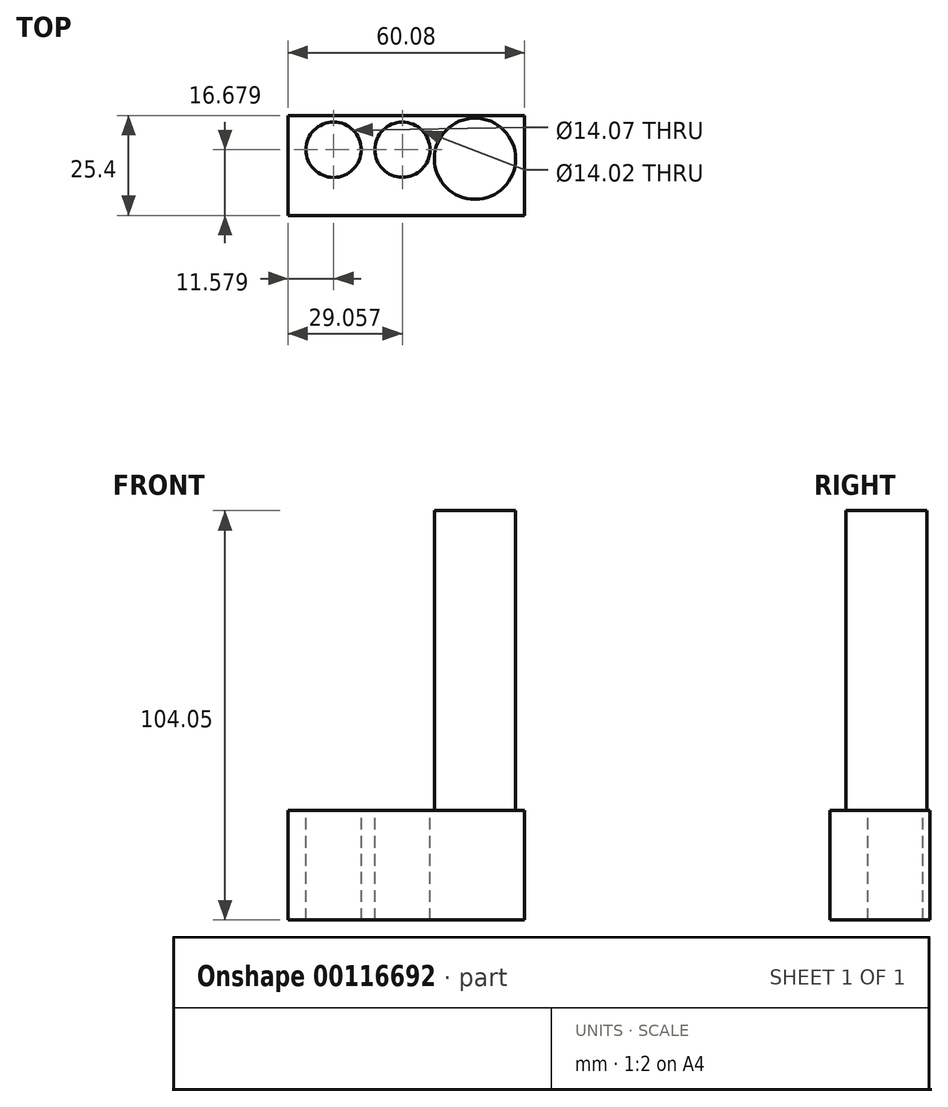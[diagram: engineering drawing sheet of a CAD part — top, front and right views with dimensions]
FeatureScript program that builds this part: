
annotation { "Feature Type Name" : "Feature", "Feature Type Description" : "" }
export const myFeature = defineFeature(function(context is Context, id is Id, definition is map)
    precondition{}
    {
        {
            var Q0;
            Q0=qCreatedBy(makeId("Front.planeOp"),FACE);
            var sketch = newSketch(context, id + "F0", { "sketchPlane" : qUnion([Q0])});
            skLineSegment(sketch, "E0.bottom", {"start": v(-24.03, 15.02) * mm, "end": v(36.05, 15.02) * mm});
            skLineSegment(sketch, "E0.top", {"start": v(-24.03, -12.83) * mm, "end": v(36.05, -12.83) * mm});
            skLineSegment(sketch, "E0.left", {"start": v(-24.03, 15.02) * mm, "end": v(-24.03, -12.83) * mm});
            skLineSegment(sketch, "E0.right", {"start": v(36.05, 15.02) * mm, "end": v(36.05, -12.83) * mm});
            skSolve(sketch);
        }
        {
            var Q0;
            Q0=makeQuery(id+"F0.imprint","IMPRINT",FACE,{"disambiguationData":[TD([[makeQuery(id+"F0.imprint","IMPRINT",EDGE,{"derivedFrom":sQuery(id+"F0.wireOp",EDGE,"E0.bottom")}),-1.0]])]});
            extrude(context, id + "F1", {"entities" : qUnion([Q0]), "depth" : 25.4 * mm});
        }
        {
            var Q0;
            Q0=makeQuery(id+"F1.opExtrude","SWEPT_FACE",FACE,{"disambiguationData":[OSD([sQuery(id+"F0.wireOp",EDGE,"E0.bottom")])]});
            var sketch = newSketch(context, id + "F2", { "sketchPlane" : qUnion([Q0])});
            skCircle(sketch, "E1", {"center": v(-12.45, -8.72) * mm, "radius": 7.04 * mm});
            skCircle(sketch, "E2", {"center": v(5.03, -8.72) * mm, "radius": 7.01 * mm});
            skCircle(sketch, "E3", {"center": v(24.03, -16.87) * mm, "radius": 3.87 * mm});
            skSolve(sketch);
        }
        {
            var Q0;
            Q0=makeQuery(id+"F2.imprint","IMPRINT",FACE,{"disambiguationData":[TD([[makeQuery(id+"F2.imprint","IMPRINT",EDGE,{"derivedFrom":sQuery(id+"F2.wireOp",EDGE,"E2")}),1.0]])]});
            var Q1;
            Q1=makeQuery(id+"F2.imprint","IMPRINT",FACE,{"disambiguationData":[TD([[makeQuery(id+"F2.imprint","IMPRINT",EDGE,{"derivedFrom":sQuery(id+"F2.wireOp",EDGE,"E1")}),1.0]])]});
            extrude(context, id + "F3", {"entities" : qUnion([Q0, Q1]), "operationType" : NewBodyOperationType.REMOVE, "oppositeDirection" : true, "depth" : 50.8 * mm});
        }
        {
            var Q0;
            Q0=makeQuery(id+"F1.opExtrude","SWEPT_FACE",FACE,{"disambiguationData":[OSD([sQuery(id+"F0.wireOp",EDGE,"E0.bottom")])]});
            var sketch = newSketch(context, id + "F4", { "sketchPlane" : qUnion([Q0])});
            skCircle(sketch, "E4", {"center": v(23.48, -11) * mm, "radius": 10.31 * mm});
            skSolve(sketch);
        }
        {
            var Q0;
            Q0=makeQuery(id+"F4.imprint","IMPRINT",FACE,{"disambiguationData":[TD([[makeQuery(id+"F4.imprint","IMPRINT",EDGE,{"derivedFrom":sQuery(id+"F4.wireOp",EDGE,"E4")}),1.0]])]});
            extrude(context, id + "F5", {"entities" : qUnion([Q0]), "operationType" : NewBodyOperationType.ADD, "depth" : 76.2 * mm});
        }
    });
